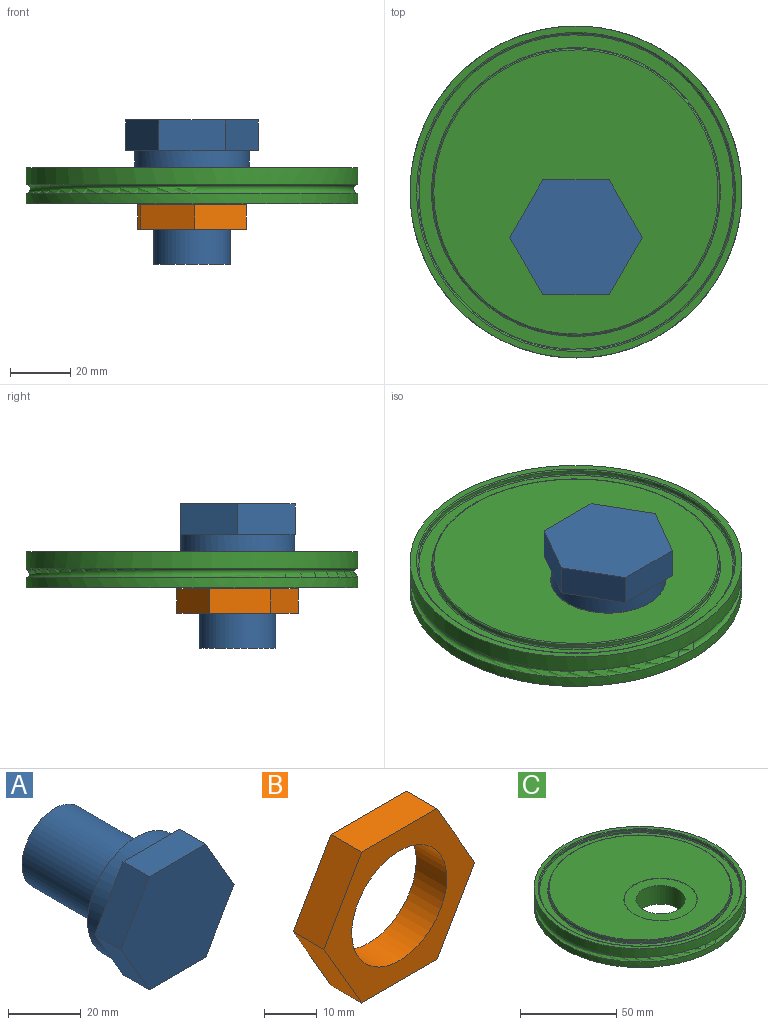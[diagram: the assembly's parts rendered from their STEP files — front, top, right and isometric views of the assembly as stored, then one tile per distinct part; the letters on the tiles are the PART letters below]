
ASSEMBLY  parts=3 mates=2
PART A: 14 faces, bbox 44x47.8x38.1 mm
  f0: cylinder r=18.92mm len=37.85mm, axis (0,1,0), area 694.6mm2, adj f5,f12
  f1: plane 25.35x25.35mm, normal (0,1,0), area 504.7mm2, adj f2
  f2: cylinder r=12.67mm len=29.85mm, axis (0,1,0), area 2376.8mm2, adj f1,f3
  f3: plane 25.35x25.35mm, normal (0,-1,0), area 94.2mm2, adj f2,f4
  f4: cylinder r=11.43mm len=22.86mm, axis (0,1,0), area 136.8mm2, adj f3,f5
  f5: plane 37.85x37.85mm, normal (0,1,0), area 714.5mm2, adj f0,f4
  f6: plane 22x10.16mm, normal (0,0,-1), area 223.5mm2, adj f7,f11,f12,f13
  f7: plane 19.05x11mm, normal (0.87,0,-0.5), area 223.5mm2, adj f6,f8,f12,f13
  f8: plane 19.05x11mm, normal (0.87,0,0.5), area 223.5mm2, adj f7,f9,f12,f13
  f9: plane 22x10.16mm, normal (0,0,1), area 223.5mm2, adj f8,f10,f12,f13
  f10: plane 19.05x11mm, normal (-0.87,0,0.5), area 223.5mm2, adj f9,f11,f12,f13
  f11: plane 19.05x11mm, normal (-0.87,0,-0.5), area 223.5mm2, adj f6,f10,f12,f13
  f12: plane 43.99x38.1mm, normal (0,1,0), area 132.2mm2, adj f0,f6,f7,f8,f9,f10,f11
  f13: plane 43.99x38.1mm, normal (0,-1,0), area 1257.1mm2, adj f6,f7,f8,f9,f10,f11
PART B: 9 faces, bbox 40.3x8.2x34.9 mm
  f0: plane 20.13x8.15mm, normal (0,0,1), area 164.2mm2, adj f1,f5,f7,f8
  f1: plane 17.44x10.07mm, normal (0.87,0,0.5), area 164.2mm2, adj f0,f2,f7,f8
  f2: plane 17.44x10.07mm, normal (0.87,0,-0.5), area 164.2mm2, adj f1,f3,f7,f8
  f3: plane 20.13x8.15mm, normal (0,0,-1), area 164.2mm2, adj f2,f4,f7,f8
  f4: plane 17.44x10.07mm, normal (-0.87,0,-0.5), area 164.2mm2, adj f3,f5,f7,f8
  f5: plane 17.44x10.07mm, normal (-0.87,0,0.5), area 164.2mm2, adj f0,f4,f7,f8
  f6: cylinder r=12.67mm len=25.35mm, axis (0,-1,0), area 649.3mm2, adj f7,f8
  f7: plane 40.27x34.87mm, normal (0,1,0), area 548.6mm2, adj f0,f1,f2,f3,f4,f5,f6
  f8: plane 40.27x34.87mm, normal (0,-1,0), area 548.6mm2, adj f0,f1,f2,f3,f4,f5,f6
PART C: 20 faces, bbox 121.3x121.3x12 mm
  f0: cylinder r=12.76mm len=25.53mm, axis (0,0,-1), area 947.2mm2, adj f7,f18
  f1: cylinder r=54.99mm len=109.98mm, axis (0,0,1), area 1211.1mm2, adj f6,f14
  f2: torus R=47.12mm, axis (0,0,-1), area 178.1mm2, adj f13,f15
  f3: cylinder r=36.68mm len=73.36mm, axis (0,0,1), area 643.9mm2, adj f4,f7
  f4: plane 83.01x83.01mm, normal (0,0,-1), area 1185.3mm2, adj f3,f5
  f5: cylinder r=41.5mm len=83.01mm, axis (0,0,1), area 728.6mm2, adj f4,f6
  f6: plane 109.98x109.98mm, normal (0,0,-1), area 4088.7mm2, adj f1,f5
  f7: plane 73.36x73.36mm, normal (0,0,-1), area 3714.4mm2, adj f0,f3
  f8: cylinder r=54.99mm len=109.98mm, axis (0,0,1), area 1878.1mm2, adj f10,f14
  f9: torus R=52.1mm, axis (0,0,1), area 196.8mm2, adj f12,f16
  f10: plane 109.98x109.98mm, normal (0,0,1), area 722.9mm2, adj f8,f17
  f11: torus R=47.88mm, axis (0,0,1), area 179.1mm2, adj f15,f16
  f12: cylinder r=52.48mm len=104.95mm, axis (0,0,1), area 418.7mm2, adj f9,f17
  f13: plane 94.23x94.23mm, normal (0,0,1), area 5834.3mm2, adj f2,f19
  f14: torus R=54.99mm, axis (0,0,-1), area 1598.5mm2, adj f1,f8
  f15: cylinder r=47.5mm len=95mm, axis (0,0,1), area 379mm2, adj f2,f11
  f16: plane 104.19x104.19mm, normal (0,0,1), area 1324.3mm2, adj f9,f11
  f17: torus R=52.86mm, axis (0,0,-1), area 197.8mm2, adj f10,f12
  f18: plane 37.85x37.85mm, normal (0,0,1), area 613.2mm2, adj f0,f19
  f19: torus R=18.92mm, axis (0,0,1), area 23.8mm2, adj f13,f18
PLACE A rot(axis=(-1,0,0),90deg) t=(8.28,-16.46,21.84)mm
PLACE B rot(axis=(0.95,-0.23,-0.23),93.2deg) t=(8.28,-16.46,-62.15)mm
PLACE C t=(8.28,-1.37,0)mm fixed
MATE cylindrical B.f6 <-> A.f0  axis (0,0,-1) through (8.28,-16.46,-14.4)mm
MATE fastened A.f0 <-> C.f0  axis (0,0,-1) through (8.28,-16.46,5.84)mm
